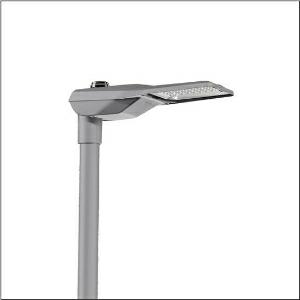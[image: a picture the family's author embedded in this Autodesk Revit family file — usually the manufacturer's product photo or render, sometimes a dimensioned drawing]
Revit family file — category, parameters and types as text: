
# Revit family: streetlight_sl_21_mini___st1_0a_5xe6d27n08jb_0e68
name_source: partatom
category: Lighting Fixtures
units: mm (PartAtom-declared; Revit-internal decimal feet)

## family parameters
Cut with Voids When Loaded = No
Host = Face
Light Source = No
Part Type = Normal
Room Calculation Point = No
Round Connector Dimension = Use Diameter
Shared = No

## types (1)
- --- (1 x LED, 10620 lm, 87.3 W, 2200K)
    Apparent Load = 87 VA
    CIE Flux Codes = 40 73 97 100 100
    Color Rendering = 70
    Color Temperature = 2200K
    Default Elevation = 1800 mm
    Description = Streetlight SL 21 mini, mast luminaire, primary light control with lens, of PMMA, primary optical cover: cover, of toughened safety glass, transparent, light distribution: ST1.0a, light emission: direct distribution, primary light characteristic: asymmetric, installation type: side-entry, LED, 3G 2.5mm², High Power LED, rated luminous flux: 10.620lm, luminous efficacy: 122lm/W, light colour: 722, colour temperature: 2200K, control gear: NEMA (7pin), control: overheat protection, pre-setting: linear dimming characteristic, constant luminous flux control, time-dependent luminous flux control, flexible luminous flux parameterisation, mains connection: 230..240V, AC, 50/60Hz, connection cable pre-assembled, cable length: 10,5m, wiring characteristics: H05VV-F, start of lifetime: 87W, end of service life: 90W, reduction: 40W, luminaire housing, of diecast aluminium (EN AC-44300), powder-coated, SITECO metallic grey (DB 702S), corrosivity category C5 high according to DIN EN ISO 12944, multi-level sealing system, sealing non-destructively replaceable, inclination adjustable: 0°, 5°, 10°, 15°, length: 628mm, width: 235mm, height: 110mm, spigot size: 42mm (side-entry), mounting height: 4..8m, protection rating (complete): IP66, insulation class (complete): insulation class I (protective earthing), certification: CE, ENEC, ENEC+, VDE, impact resistance: IK10, permissible operating ambient temperature for outdoor applications: -40..+50°C, standard-compliant lighting for roads and squares, packaging unit: 1 piece

Light Distribution: ST1.0a
    Height = 110 mm
    Lamp = 1 x LED
    Lamp Light Flux = 10620 lm
    Lamp Power = 87.3 W
    Lamp count = 1
    Length = 625 mm
    Luminous efficacy = 122 lm/W
    Manufacturer = Siteco
    ModVariant = No
    Model = 5XE6D27N08JB
    Number of Poles = 1
    OnlyDefault = Yes
    Power Factor = 1
    Product Name = Streetlight SL 21 mini | ST1.0a
    Product group = mast luminaire | pylon top
    ProductGroupID = 6100
    Protection Class = Protection class I
    Protection Degree = IP 66
    RLX_Detail_Level = 1
    RLX_Emergency_Light_Flux = 0 lm
    RLX_Emergency_Type = 0
    RLX_Emergency_Type_DB = No
    RlxData = <blob elided: 25997 chars, md5=4b7bca4b>
    Socket = socket
    Standby Power = 0 W
    System Light Flux = 10620 lm
    System Power = 87 W
    Type Comments = factory setting: luminous flux: 100 % | dim-lin: 254 | 915 mA
    Type Image = l_1294379.jpg
    URL = http://relux.com
    VarID = @adj_134897
    Voltage = 0 V
    Weight = 0.00 kg
    Width = 234 mm

## geometry (parser evidence)
native form markers: Blend x4, Sweep x11
no freeform markers — native parametric forms only
